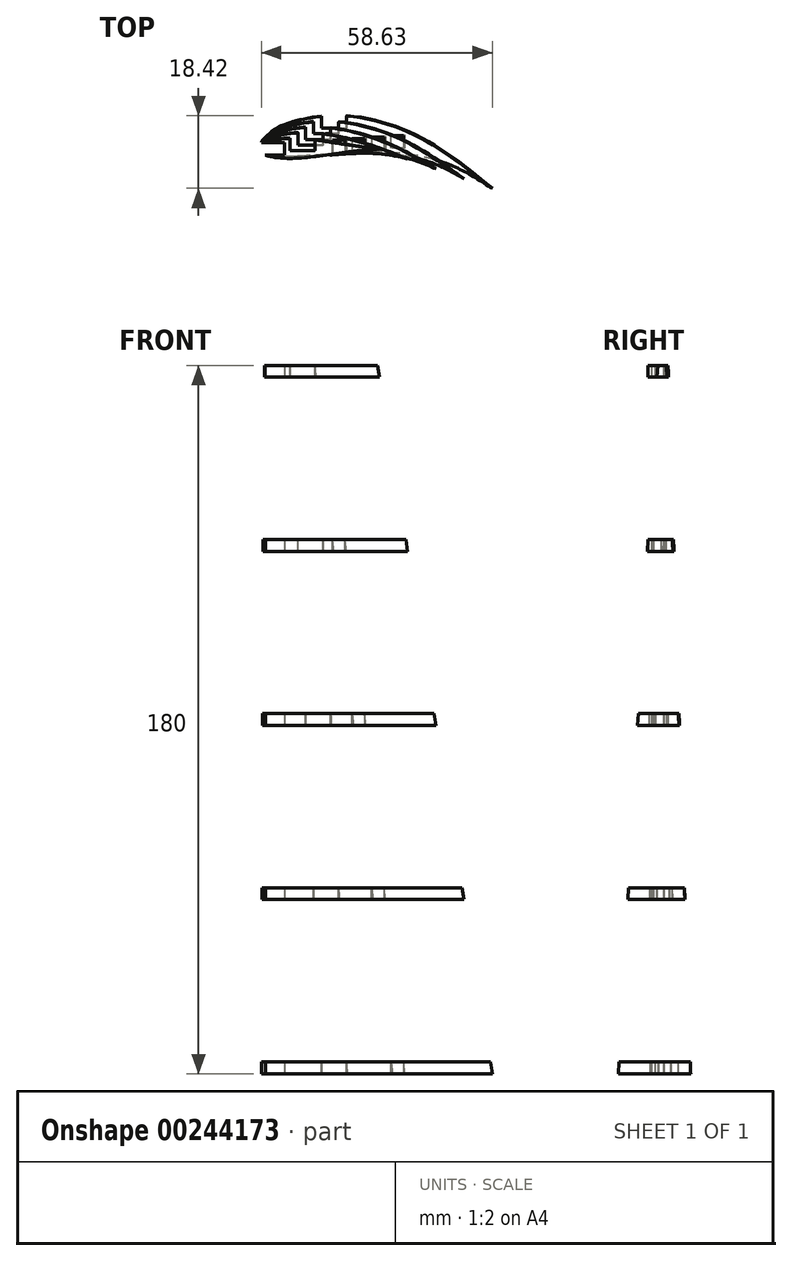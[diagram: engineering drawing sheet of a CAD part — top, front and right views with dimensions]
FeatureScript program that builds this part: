
annotation { "Feature Type Name" : "Feature", "Feature Type Description" : "" }
export const myFeature = defineFeature(function(context is Context, id is Id, definition is map)
    precondition{}
    {
        {
            var Q0;
            Q0=qCreatedBy(makeId("Top.planeOp"),FACE);
            var sketch = newSketch(context, id + "F0", { "sketchPlane" : qUnion([Q0])});
            skLineSegment(sketch, "E0", {"start": v(0.56, 2.05) * mm, "end": v(2.04, 3.44) * mm});
            skLineSegment(sketch, "E1", {"start": v(2.04, 3.44) * mm, "end": v(2.8, 4.09) * mm});
            skLineSegment(sketch, "E2", {"start": v(2.8, 4.09) * mm, "end": v(3.82, 4.84) * mm});
            skLineSegment(sketch, "E3", {"start": v(3.82, 4.84) * mm, "end": v(4.45, 5.23) * mm});
            skLineSegment(sketch, "E4", {"start": v(4.45, 5.23) * mm, "end": v(5.33, 5.7) * mm});
            skLineSegment(sketch, "E5", {"start": v(5.33, 5.7) * mm, "end": v(6.25, 6.12) * mm});
            skLineSegment(sketch, "E6", {"start": v(6.25, 6.12) * mm, "end": v(7.2, 6.48) * mm});
            skLineSegment(sketch, "E7", {"start": v(7.2, 6.48) * mm, "end": v(8.16, 6.8) * mm});
            skLineSegment(sketch, "E8", {"start": v(8.16, 6.8) * mm, "end": v(9.34, 7.15) * mm});
            skLineSegment(sketch, "E9", {"start": v(9.34, 7.15) * mm, "end": v(10.11, 7.36) * mm});
            skLineSegment(sketch, "E10", {"start": v(10.11, 7.36) * mm, "end": v(11.1, 7.6) * mm});
            skLineSegment(sketch, "E11", {"start": v(11.1, 7.6) * mm, "end": v(12.08, 7.8) * mm});
            skLineSegment(sketch, "E12", {"start": v(12.08, 7.8) * mm, "end": v(13.07, 7.98) * mm});
            skLineSegment(sketch, "E13", {"start": v(13.07, 7.98) * mm, "end": v(14.07, 8.14) * mm});
            skLineSegment(sketch, "E14", {"start": v(14.07, 8.14) * mm, "end": v(15.06, 8.26) * mm});
            skLineSegment(sketch, "E15", {"start": v(15.06, 8.26) * mm, "end": v(16.06, 8.36) * mm});
            skLineSegment(sketch, "E16", {"start": v(16.06, 8.36) * mm, "end": v(16.57, 8.4) * mm});
            skLineSegment(sketch, "E17", {"start": v(16.57, 8.4) * mm, "end": v(18.07, 8.47) * mm});
            skLineSegment(sketch, "E18", {"start": v(18.07, 8.47) * mm, "end": v(19.07, 8.48) * mm});
            skLineSegment(sketch, "E19", {"start": v(19.07, 8.48) * mm, "end": v(20.08, 8.46) * mm});
            skLineSegment(sketch, "E20", {"start": v(20.08, 8.46) * mm, "end": v(21.09, 8.42) * mm});
            skLineSegment(sketch, "E21", {"start": v(21.09, 8.42) * mm, "end": v(23.1, 8.25) * mm});
            skLineSegment(sketch, "E22", {"start": v(23.1, 8.25) * mm, "end": v(24.82, 8.04) * mm});
            skLineSegment(sketch, "E23", {"start": v(24.82, 8.04) * mm, "end": v(27.09, 7.66) * mm});
            skLineSegment(sketch, "E24", {"start": v(27.09, 7.66) * mm, "end": v(29.05, 7.24) * mm});
            skLineSegment(sketch, "E25", {"start": v(29.05, 7.24) * mm, "end": v(31, 6.74) * mm});
            skLineSegment(sketch, "E26", {"start": v(31, 6.74) * mm, "end": v(33.36, 6.03) * mm});
            skLineSegment(sketch, "E27", {"start": v(33.36, 6.03) * mm, "end": v(34.84, 5.51) * mm});
            skLineSegment(sketch, "E28", {"start": v(34.84, 5.51) * mm, "end": v(36.73, 4.8) * mm});
            skLineSegment(sketch, "E29", {"start": v(36.73, 4.8) * mm, "end": v(38.58, 4) * mm});
            skLineSegment(sketch, "E30", {"start": v(38.58, 4) * mm, "end": v(40.4, 3.16) * mm});
            skLineSegment(sketch, "E31", {"start": v(40.4, 3.16) * mm, "end": v(41.54, 2.59) * mm});
            skLineSegment(sketch, "E32", {"start": v(41.54, 2.59) * mm, "end": v(43.94, 1.28) * mm});
            skLineSegment(sketch, "E33", {"start": v(43.94, 1.28) * mm, "end": v(45.67, 0.26) * mm});
            skLineSegment(sketch, "E34", {"start": v(45.67, 0.26) * mm, "end": v(47.37, -0.82) * mm});
            skLineSegment(sketch, "E35", {"start": v(47.37, -0.82) * mm, "end": v(48.77, -1.74) * mm});
            skLineSegment(sketch, "E36", {"start": v(48.77, -1.74) * mm, "end": v(50.75, -3.11) * mm});
            skLineSegment(sketch, "E37", {"start": v(50.75, -3.11) * mm, "end": v(52.4, -4.32) * mm});
            skLineSegment(sketch, "E38", {"start": v(52.4, -4.32) * mm, "end": v(54.53, -6.01) * mm});
            skLineSegment(sketch, "E39", {"start": v(54.53, -6.01) * mm, "end": v(55.4, -6.76) * mm});
            skLineSegment(sketch, "E40", {"start": v(55.4, -6.76) * mm, "end": v(56.12, -7.39) * mm});
            skLineSegment(sketch, "E41", {"start": v(56.12, -7.39) * mm, "end": v(56.86, -8.05) * mm});
            skLineSegment(sketch, "E42", {"start": v(56.86, -8.05) * mm, "end": v(57.66, -8.75) * mm});
            skLineSegment(sketch, "E43", {"start": v(57.66, -8.75) * mm, "end": v(58.2, -9.21) * mm});
            skLineSegment(sketch, "E44", {"start": v(58.2, -9.21) * mm, "end": v(58.75, -9.68) * mm});
            skLineSegment(sketch, "E45", {"start": v(58.75, -9.68) * mm, "end": v(58.92, -9.83) * mm});
            skLineSegment(sketch, "E46", {"start": v(58.92, -9.83) * mm, "end": v(59.03, -9.93) * mm});
            skLineSegment(sketch, "E47", {"start": v(59.03, -9.93) * mm, "end": v(59.12, -10) * mm});
            skLineSegment(sketch, "E48", {"start": v(59.12, -10) * mm, "end": v(59.13, -10.04) * mm});
            skLineSegment(sketch, "E49", {"start": v(59.13, -10.04) * mm, "end": v(59.1, -10.02) * mm});
            skLineSegment(sketch, "E50", {"start": v(59.1, -10.02) * mm, "end": v(59, -9.97) * mm});
            skLineSegment(sketch, "E51", {"start": v(59, -9.97) * mm, "end": v(58.88, -9.89) * mm});
            skLineSegment(sketch, "E52", {"start": v(58.88, -9.89) * mm, "end": v(58.71, -9.78) * mm});
            skLineSegment(sketch, "E53", {"start": v(58.71, -9.78) * mm, "end": v(58.5, -9.64) * mm});
            skLineSegment(sketch, "E54", {"start": v(58.5, -9.64) * mm, "end": v(58.27, -9.48) * mm});
            skLineSegment(sketch, "E55", {"start": v(58.27, -9.48) * mm, "end": v(58.01, -9.3) * mm});
            skLineSegment(sketch, "E56", {"start": v(58.01, -9.3) * mm, "end": v(57.42, -8.88) * mm});
            skLineSegment(sketch, "E57", {"start": v(57.42, -8.88) * mm, "end": v(56.77, -8.43) * mm});
            skLineSegment(sketch, "E58", {"start": v(56.77, -8.43) * mm, "end": v(55.48, -7.55) * mm});
            skLineSegment(sketch, "E59", {"start": v(55.48, -7.55) * mm, "end": v(54.79, -7.1) * mm});
            skLineSegment(sketch, "E60", {"start": v(54.79, -7.1) * mm, "end": v(54.18, -6.73) * mm});
            skLineSegment(sketch, "E61", {"start": v(54.18, -6.73) * mm, "end": v(53.6, -6.38) * mm});
            skLineSegment(sketch, "E62", {"start": v(53.6, -6.38) * mm, "end": v(53.05, -6.06) * mm});
            skLineSegment(sketch, "E63", {"start": v(53.05, -6.06) * mm, "end": v(52.53, -5.78) * mm});
            skLineSegment(sketch, "E64", {"start": v(52.53, -5.78) * mm, "end": v(52.03, -5.52) * mm});
            skLineSegment(sketch, "E65", {"start": v(52.03, -5.52) * mm, "end": v(51.55, -5.29) * mm});
            skLineSegment(sketch, "E66", {"start": v(51.55, -5.29) * mm, "end": v(51.1, -5.08) * mm});
            skLineSegment(sketch, "E67", {"start": v(51.1, -5.08) * mm, "end": v(50.22, -4.72) * mm});
            skLineSegment(sketch, "E68", {"start": v(50.22, -4.72) * mm, "end": v(49.4, -4.43) * mm});
            skLineSegment(sketch, "E69", {"start": v(49.4, -4.43) * mm, "end": v(48.61, -4.18) * mm});
            skLineSegment(sketch, "E70", {"start": v(48.61, -4.18) * mm, "end": v(47.04, -3.79) * mm});
            skLineSegment(sketch, "E71", {"start": v(47.04, -3.79) * mm, "end": v(46.4, -3.64) * mm});
            skLineSegment(sketch, "E72", {"start": v(46.4, -3.64) * mm, "end": v(45.37, -3.4) * mm});
            skLineSegment(sketch, "E73", {"start": v(45.37, -3.4) * mm, "end": v(44.49, -3.2) * mm});
            skLineSegment(sketch, "E74", {"start": v(44.49, -3.2) * mm, "end": v(43.57, -2.98) * mm});
            skLineSegment(sketch, "E75", {"start": v(43.57, -2.98) * mm, "end": v(41.64, -2.54) * mm});
            skLineSegment(sketch, "E76", {"start": v(41.64, -2.54) * mm, "end": v(39.63, -2.11) * mm});
            skLineSegment(sketch, "E77", {"start": v(39.63, -2.11) * mm, "end": v(37.56, -1.7) * mm});
            skLineSegment(sketch, "E78", {"start": v(37.56, -1.7) * mm, "end": v(35.47, -1.36) * mm});
            skLineSegment(sketch, "E79", {"start": v(35.47, -1.36) * mm, "end": v(33, -1.03) * mm});
            skLineSegment(sketch, "E80", {"start": v(33, -1.03) * mm, "end": v(31.32, -0.88) * mm});
            skLineSegment(sketch, "E81", {"start": v(31.32, -0.88) * mm, "end": v(29.29, -0.77) * mm});
            skLineSegment(sketch, "E82", {"start": v(29.29, -0.77) * mm, "end": v(27.28, -0.73) * mm});
            skLineSegment(sketch, "E83", {"start": v(27.28, -0.73) * mm, "end": v(25.28, -0.76) * mm});
            skLineSegment(sketch, "E84", {"start": v(25.28, -0.76) * mm, "end": v(23.3, -0.83) * mm});
            skLineSegment(sketch, "E85", {"start": v(23.3, -0.83) * mm, "end": v(19.54, -1.03) * mm});
            skLineSegment(sketch, "E86", {"start": v(19.54, -1.03) * mm, "end": v(17.26, -1.18) * mm});
            skLineSegment(sketch, "E87", {"start": v(17.26, -1.18) * mm, "end": v(13.22, -1.47) * mm});
            skLineSegment(sketch, "E88", {"start": v(13.22, -1.47) * mm, "end": v(11.22, -1.65) * mm});
            skLineSegment(sketch, "E89", {"start": v(11.22, -1.65) * mm, "end": v(9.16, -1.86) * mm});
            skLineSegment(sketch, "E90", {"start": v(9.16, -1.86) * mm, "end": v(7.34, -2.05) * mm});
            skLineSegment(sketch, "E91", {"start": v(7.34, -2.05) * mm, "end": v(6.37, -2.12) * mm});
            skLineSegment(sketch, "E92", {"start": v(6.37, -2.12) * mm, "end": v(5.38, -2.14) * mm});
            skLineSegment(sketch, "E93", {"start": v(5.38, -2.14) * mm, "end": v(4.35, -2.1) * mm});
            skLineSegment(sketch, "E94", {"start": v(4.35, -2.1) * mm, "end": v(3.82, -2.04) * mm});
            skLineSegment(sketch, "E95", {"start": v(3.82, -2.04) * mm, "end": v(3.28, -1.96) * mm});
            skLineSegment(sketch, "E96", {"start": v(3.28, -1.96) * mm, "end": v(2.76, -1.86) * mm});
            skLineSegment(sketch, "E97", {"start": v(2.76, -1.86) * mm, "end": v(2.16, -1.72) * mm});
            skLineSegment(sketch, "E98", {"start": v(2.16, -1.72) * mm, "end": v(1.6, -1.55) * mm});
            skLineSegment(sketch, "E99", {"start": v(1.6, -1.55) * mm, "end": v(1.1, -1.34) * mm});
            skLineSegment(sketch, "E100", {"start": v(1.1, -1.34) * mm, "end": v(0.65, -1.09) * mm});
            skLineSegment(sketch, "E101", {"start": v(0.65, -1.09) * mm, "end": v(0.47, -0.94) * mm});
            skLineSegment(sketch, "E102", {"start": v(0.47, -0.94) * mm, "end": v(0.3, -0.78) * mm});
            skLineSegment(sketch, "E103", {"start": v(0.3, -0.78) * mm, "end": v(0.18, -0.6) * mm});
            skLineSegment(sketch, "E104", {"start": v(0.18, -0.6) * mm, "end": v(0.09, -0.44) * mm});
            skLineSegment(sketch, "E105", {"start": v(0.09, -0.44) * mm, "end": v(0.02, -0.22) * mm});
            skLineSegment(sketch, "E106", {"start": v(0.02, -0.22) * mm, "end": v(0, 0) * mm});
            skLineSegment(sketch, "E107", {"start": v(0, 0) * mm, "end": v(0, 0.23) * mm});
            skLineSegment(sketch, "E108", {"start": v(0, 0.23) * mm, "end": v(0.04, 0.47) * mm});
            skLineSegment(sketch, "E109", {"start": v(0.04, 0.47) * mm, "end": v(0.16, 0.98) * mm});
            skLineSegment(sketch, "E110", {"start": v(0.16, 0.98) * mm, "end": v(0.35, 1.5) * mm});
            skLineSegment(sketch, "E111", {"start": v(0.35, 1.5) * mm, "end": v(0.56, 2.05) * mm});
            skSolve(sketch);
        }
        {
            var Q0;
            Q0=qCreatedBy(makeId("Top.planeOp"),FACE);
            var sketch = newSketch(context, id + "F1", { "sketchPlane" : qUnion([Q0])});
            skPoint(sketch, "E112.0", {"position": v(0, 0) * mm});
            skPoint(sketch, "E112.1", {"position": v(0.16, 0.98) * mm});
            skPoint(sketch, "E112.2", {"position": v(5.33, 5.7) * mm});
            skPoint(sketch, "E112.3", {"position": v(19.07, 8.48) * mm});
            skPoint(sketch, "E112.4", {"position": v(40.4, 3.16) * mm});
            skPoint(sketch, "E112.5", {"position": v(59.13, -10.04) * mm});
            skPoint(sketch, "E112.6", {"position": v(27.28, -0.73) * mm});
            skPoint(sketch, "E112.7", {"position": v(2.76, -1.86) * mm});
            skPoint(sketch, "E112.8", {"position": v(0.18, -0.6) * mm});
            skPoint(sketch, "E112.9", {"position": v(0.65, -1.09) * mm});
            skFitSpline(sketch, "E113", {"points": [v(0, 0) * mm, v(0.18, -0.6) * mm, v(0.65, -1.09) * mm, v(2.76, -1.86) * mm, v(27.28, -0.73) * mm, v(59.13, -10.04) * mm], "startDerivative": vector(2.05, -11.29) * mm, "endDerivative": vector(81.04, -57.95) * mm});
            skPoint(sketch, "E114.0", {"position": v(2.04, 3.44) * mm});
            skFitSpline(sketch, "E115", {"points": [v(0, 0) * mm, v(0.16, 0.98) * mm, v(2.04, 3.44) * mm, v(5.33, 5.7) * mm, v(19.07, 8.48) * mm, v(40.4, 3.16) * mm, v(59.13, -10.04) * mm], "startDerivative": vector(-0.04, 15.95) * mm, "endDerivative": vector(66.9, -54.86) * mm});
            skSolve(sketch);
        }
        {
            var Q0;
            Q0=qCreatedBy(makeId("Top.planeOp"),FACE);
            cPlane(context, id + "F2", {"entities" : qUnion([Q0]), "cplaneType" : CPlaneType.OFFSET, "offset" : 180 * mm, "width" : 150 * mm, "height" : 150 * mm});
        }
        {
            var Q0;
            Q0=qCreatedBy(id+"F2.planeOp",FACE);
            var sketch = newSketch(context, id + "F3", { "sketchPlane" : qUnion([Q0])});
            skLineSegment(sketch, "E116", {"start": v(0, 0) * mm, "end": v(0.23, 0.44) * mm});
            skLineSegment(sketch, "E117", {"start": v(0.23, 0.44) * mm, "end": v(0.36, 0.65) * mm});
            skLineSegment(sketch, "E118", {"start": v(0.36, 0.65) * mm, "end": v(0.5, 0.85) * mm});
            skLineSegment(sketch, "E119", {"start": v(0.5, 0.85) * mm, "end": v(0.64, 1.04) * mm});
            skLineSegment(sketch, "E120", {"start": v(0.64, 1.04) * mm, "end": v(0.77, 1.18) * mm});
            skLineSegment(sketch, "E121", {"start": v(0.77, 1.18) * mm, "end": v(0.98, 1.36) * mm});
            skLineSegment(sketch, "E122", {"start": v(0.98, 1.36) * mm, "end": v(1.17, 1.5) * mm});
            skLineSegment(sketch, "E123", {"start": v(1.17, 1.5) * mm, "end": v(1.38, 1.62) * mm});
            skLineSegment(sketch, "E124", {"start": v(1.38, 1.62) * mm, "end": v(1.6, 1.72) * mm});
            skLineSegment(sketch, "E125", {"start": v(1.6, 1.72) * mm, "end": v(1.82, 1.81) * mm});
            skLineSegment(sketch, "E126", {"start": v(1.82, 1.81) * mm, "end": v(2.06, 1.9) * mm});
            skLineSegment(sketch, "E127", {"start": v(2.06, 1.9) * mm, "end": v(2.55, 2.03) * mm});
            skLineSegment(sketch, "E128", {"start": v(2.55, 2.03) * mm, "end": v(2.95, 2.13) * mm});
            skLineSegment(sketch, "E129", {"start": v(2.95, 2.13) * mm, "end": v(3.53, 2.24) * mm});
            skLineSegment(sketch, "E130", {"start": v(3.53, 2.24) * mm, "end": v(4.01, 2.33) * mm});
            skLineSegment(sketch, "E131", {"start": v(4.01, 2.33) * mm, "end": v(4.97, 2.47) * mm});
            skLineSegment(sketch, "E132", {"start": v(4.97, 2.47) * mm, "end": v(5.92, 2.57) * mm});
            skLineSegment(sketch, "E133", {"start": v(5.92, 2.57) * mm, "end": v(6.44, 2.6) * mm});
            skLineSegment(sketch, "E134", {"start": v(6.44, 2.6) * mm, "end": v(7.84, 2.63) * mm});
            skLineSegment(sketch, "E135", {"start": v(7.84, 2.63) * mm, "end": v(8.81, 2.62) * mm});
            skLineSegment(sketch, "E136", {"start": v(8.81, 2.62) * mm, "end": v(9.78, 2.58) * mm});
            skLineSegment(sketch, "E137", {"start": v(9.78, 2.58) * mm, "end": v(10.87, 2.51) * mm});
            skLineSegment(sketch, "E138", {"start": v(10.87, 2.51) * mm, "end": v(11.73, 2.44) * mm});
            skLineSegment(sketch, "E139", {"start": v(11.73, 2.44) * mm, "end": v(12.7, 2.36) * mm});
            skLineSegment(sketch, "E140", {"start": v(12.7, 2.36) * mm, "end": v(13.67, 2.26) * mm});
            skLineSegment(sketch, "E141", {"start": v(13.67, 2.26) * mm, "end": v(14.63, 2.14) * mm});
            skLineSegment(sketch, "E142", {"start": v(14.63, 2.14) * mm, "end": v(15.89, 1.98) * mm});
            skLineSegment(sketch, "E143", {"start": v(15.89, 1.98) * mm, "end": v(16.53, 1.89) * mm});
            skLineSegment(sketch, "E144", {"start": v(16.53, 1.89) * mm, "end": v(18.42, 1.6) * mm});
            skLineSegment(sketch, "E145", {"start": v(18.42, 1.6) * mm, "end": v(19.38, 1.44) * mm});
            skLineSegment(sketch, "E146", {"start": v(19.38, 1.44) * mm, "end": v(20.35, 1.28) * mm});
            skLineSegment(sketch, "E147", {"start": v(20.35, 1.28) * mm, "end": v(21, 1.18) * mm});
            skLineSegment(sketch, "E148", {"start": v(21, 1.18) * mm, "end": v(22.34, 0.98) * mm});
            skLineSegment(sketch, "E149", {"start": v(22.34, 0.98) * mm, "end": v(23.33, 0.83) * mm});
            skLineSegment(sketch, "E150", {"start": v(23.33, 0.83) * mm, "end": v(24.3, 0.68) * mm});
            skLineSegment(sketch, "E151", {"start": v(24.3, 0.68) * mm, "end": v(24.75, 0.61) * mm});
            skLineSegment(sketch, "E152", {"start": v(24.75, 0.61) * mm, "end": v(25.2, 0.54) * mm});
            skLineSegment(sketch, "E153", {"start": v(25.2, 0.54) * mm, "end": v(25.57, 0.47) * mm});
            skLineSegment(sketch, "E154", {"start": v(25.57, 0.47) * mm, "end": v(26.03, 0.39) * mm});
            skLineSegment(sketch, "E155", {"start": v(26.03, 0.39) * mm, "end": v(26.44, 0.32) * mm});
            skLineSegment(sketch, "E156", {"start": v(26.44, 0.32) * mm, "end": v(26.87, 0.25) * mm});
            skLineSegment(sketch, "E157", {"start": v(26.87, 0.25) * mm, "end": v(27.33, 0.19) * mm});
            skLineSegment(sketch, "E158", {"start": v(27.33, 0.19) * mm, "end": v(27.57, 0.16) * mm});
            skLineSegment(sketch, "E159", {"start": v(27.57, 0.16) * mm, "end": v(27.84, 0.13) * mm});
            skLineSegment(sketch, "E160", {"start": v(27.84, 0.13) * mm, "end": v(28.12, 0.1) * mm});
            skLineSegment(sketch, "E161", {"start": v(28.12, 0.1) * mm, "end": v(28.42, 0.08) * mm});
            skLineSegment(sketch, "E162", {"start": v(28.42, 0.08) * mm, "end": v(28.8, 0.06) * mm});
            skLineSegment(sketch, "E163", {"start": v(28.8, 0.06) * mm, "end": v(29.09, 0.04) * mm});
            skLineSegment(sketch, "E164", {"start": v(29.09, 0.04) * mm, "end": v(29.42, 0.03) * mm});
            skLineSegment(sketch, "E165", {"start": v(29.42, 0.03) * mm, "end": v(29.57, 0.02) * mm});
            skLineSegment(sketch, "E166", {"start": v(29.57, 0.02) * mm, "end": v(29.71, 0.02) * mm});
            skLineSegment(sketch, "E167", {"start": v(29.71, 0.02) * mm, "end": v(29.83, 0.01) * mm});
            skLineSegment(sketch, "E168", {"start": v(29.83, 0.01) * mm, "end": v(29.92, 0) * mm});
            skLineSegment(sketch, "E169", {"start": v(29.92, 0) * mm, "end": v(29.98, 0) * mm});
            skLineSegment(sketch, "E170", {"start": v(29.98, 0) * mm, "end": v(30, 0) * mm});
            skLineSegment(sketch, "E171", {"start": v(30, 0) * mm, "end": v(29.99, 0) * mm});
            skLineSegment(sketch, "E172", {"start": v(29.99, 0) * mm, "end": v(29.94, 0) * mm});
            skLineSegment(sketch, "E173", {"start": v(29.94, 0) * mm, "end": v(29.85, 0) * mm});
            skLineSegment(sketch, "E174", {"start": v(29.85, 0) * mm, "end": v(29.74, -0.01) * mm});
            skLineSegment(sketch, "E175", {"start": v(29.74, -0.01) * mm, "end": v(29.61, -0.01) * mm});
            skLineSegment(sketch, "E176", {"start": v(29.61, -0.01) * mm, "end": v(29.46, -0.02) * mm});
            skLineSegment(sketch, "E177", {"start": v(29.46, -0.02) * mm, "end": v(29.13, -0.02) * mm});
            skLineSegment(sketch, "E178", {"start": v(29.13, -0.02) * mm, "end": v(28.9, -0.03) * mm});
            skLineSegment(sketch, "E179", {"start": v(28.9, -0.03) * mm, "end": v(28.49, -0.04) * mm});
            skLineSegment(sketch, "E180", {"start": v(28.49, -0.04) * mm, "end": v(28.2, -0.06) * mm});
            skLineSegment(sketch, "E181", {"start": v(28.2, -0.06) * mm, "end": v(27.92, -0.07) * mm});
            skLineSegment(sketch, "E182", {"start": v(27.92, -0.07) * mm, "end": v(27.66, -0.1) * mm});
            skLineSegment(sketch, "E183", {"start": v(27.66, -0.1) * mm, "end": v(27.41, -0.11) * mm});
            skLineSegment(sketch, "E184", {"start": v(27.41, -0.11) * mm, "end": v(26.95, -0.16) * mm});
            skLineSegment(sketch, "E185", {"start": v(26.95, -0.16) * mm, "end": v(26.52, -0.2) * mm});
            skLineSegment(sketch, "E186", {"start": v(26.52, -0.2) * mm, "end": v(26.11, -0.27) * mm});
            skLineSegment(sketch, "E187", {"start": v(26.11, -0.27) * mm, "end": v(25.7, -0.32) * mm});
            skLineSegment(sketch, "E188", {"start": v(25.7, -0.32) * mm, "end": v(25.26, -0.39) * mm});
            skLineSegment(sketch, "E189", {"start": v(25.26, -0.39) * mm, "end": v(24.8, -0.45) * mm});
            skLineSegment(sketch, "E190", {"start": v(24.8, -0.45) * mm, "end": v(24.34, -0.51) * mm});
            skLineSegment(sketch, "E191", {"start": v(24.34, -0.51) * mm, "end": v(23.38, -0.65) * mm});
            skLineSegment(sketch, "E192", {"start": v(23.38, -0.65) * mm, "end": v(22.38, -0.79) * mm});
            skLineSegment(sketch, "E193", {"start": v(22.38, -0.79) * mm, "end": v(21.08, -0.97) * mm});
            skLineSegment(sketch, "E194", {"start": v(21.08, -0.97) * mm, "end": v(20.4, -1.08) * mm});
            skLineSegment(sketch, "E195", {"start": v(20.4, -1.08) * mm, "end": v(18.47, -1.37) * mm});
            skLineSegment(sketch, "E196", {"start": v(18.47, -1.37) * mm, "end": v(15.89, -1.74) * mm});
            skLineSegment(sketch, "E197", {"start": v(15.89, -1.74) * mm, "end": v(14.67, -1.9) * mm});
            skLineSegment(sketch, "E198", {"start": v(14.67, -1.9) * mm, "end": v(12.75, -2.12) * mm});
            skLineSegment(sketch, "E199", {"start": v(12.75, -2.12) * mm, "end": v(10.8, -2.3) * mm});
            skLineSegment(sketch, "E200", {"start": v(10.8, -2.3) * mm, "end": v(9.83, -2.38) * mm});
            skLineSegment(sketch, "E201", {"start": v(9.83, -2.38) * mm, "end": v(8.86, -2.44) * mm});
            skLineSegment(sketch, "E202", {"start": v(8.86, -2.44) * mm, "end": v(7.89, -2.47) * mm});
            skLineSegment(sketch, "E203", {"start": v(7.89, -2.47) * mm, "end": v(6.93, -2.47) * mm});
            skLineSegment(sketch, "E204", {"start": v(6.93, -2.47) * mm, "end": v(6.35, -2.45) * mm});
            skLineSegment(sketch, "E205", {"start": v(6.35, -2.45) * mm, "end": v(5.02, -2.34) * mm});
            skLineSegment(sketch, "E206", {"start": v(5.02, -2.34) * mm, "end": v(4.06, -2.21) * mm});
            skLineSegment(sketch, "E207", {"start": v(4.06, -2.21) * mm, "end": v(2.9, -2) * mm});
            skLineSegment(sketch, "E208", {"start": v(2.9, -2) * mm, "end": v(2.6, -1.95) * mm});
            skLineSegment(sketch, "E209", {"start": v(2.6, -1.95) * mm, "end": v(2.1, -1.83) * mm});
            skLineSegment(sketch, "E210", {"start": v(2.1, -1.83) * mm, "end": v(1.85, -1.76) * mm});
            skLineSegment(sketch, "E211", {"start": v(1.85, -1.76) * mm, "end": v(1.62, -1.68) * mm});
            skLineSegment(sketch, "E212", {"start": v(1.62, -1.68) * mm, "end": v(1.4, -1.58) * mm});
            skLineSegment(sketch, "E213", {"start": v(1.4, -1.58) * mm, "end": v(1.18, -1.47) * mm});
            skLineSegment(sketch, "E214", {"start": v(1.18, -1.47) * mm, "end": v(0.98, -1.35) * mm});
            skLineSegment(sketch, "E215", {"start": v(0.98, -1.35) * mm, "end": v(0.8, -1.2) * mm});
            skLineSegment(sketch, "E216", {"start": v(0.8, -1.2) * mm, "end": v(0.7, -1.12) * mm});
            skLineSegment(sketch, "E217", {"start": v(0.7, -1.12) * mm, "end": v(0.48, -0.86) * mm});
            skLineSegment(sketch, "E218", {"start": v(0.48, -0.86) * mm, "end": v(0.35, -0.66) * mm});
            skLineSegment(sketch, "E219", {"start": v(0.35, -0.66) * mm, "end": v(0.23, -0.44) * mm});
            skLineSegment(sketch, "E220", {"start": v(0.23, -0.44) * mm, "end": v(0, 0) * mm});
            skSolve(sketch);
        }
        {
            var Q0;
            Q0=qCreatedBy(id+"F2.planeOp",FACE);
            var sketch = newSketch(context, id + "F4", { "sketchPlane" : qUnion([Q0])});
            skPoint(sketch, "E221.0", {"position": v(0, 0) * mm});
            skPoint(sketch, "E221.1", {"position": v(0.36, 0.65) * mm});
            skPoint(sketch, "E221.2", {"position": v(0.77, 1.18) * mm});
            skPoint(sketch, "E221.3", {"position": v(1.38, 1.62) * mm});
            skPoint(sketch, "E221.4", {"position": v(0.35, -0.66) * mm});
            skPoint(sketch, "E221.5", {"position": v(0.8, -1.2) * mm});
            skPoint(sketch, "E221.6", {"position": v(1.62, -1.68) * mm});
            skPoint(sketch, "E221.7", {"position": v(7.89, -2.47) * mm});
            skPoint(sketch, "E221.8", {"position": v(7.84, 2.63) * mm});
            skPoint(sketch, "E221.9", {"position": v(21, 1.18) * mm});
            skPoint(sketch, "E221.10", {"position": v(21.08, -0.97) * mm});
            skPoint(sketch, "E221.11", {"position": v(30, 0) * mm});
            skFitSpline(sketch, "E222", {"points": [v(0, 0) * mm, v(0.36, 0.65) * mm, v(0.77, 1.18) * mm, v(1.38, 1.62) * mm, v(7.84, 2.63) * mm, v(21, 1.18) * mm, v(30, 0) * mm], "startDerivative": vector(4.6, 9.1) * mm, "endDerivative": vector(32.93, -3.87) * mm});
            skFitSpline(sketch, "E223", {"points": [v(0, 0) * mm, v(0.35, -0.66) * mm, v(0.8, -1.2) * mm, v(1.62, -1.68) * mm, v(7.89, -2.47) * mm, v(21.08, -0.97) * mm, v(30, 0) * mm], "startDerivative": vector(4.5, -9.21) * mm, "endDerivative": vector(32.84, 2.96) * mm});
            skSolve(sketch);
        }
        {
            var Q0;
            Q0 = qSketchRegion(id + "F4", true);
            var Q1;
            Q1 = qSketchRegion(id + "F1", true);
            loft(context, id + "F5", {"sheetProfilesArray" : [{ "sheetProfileEntities" : qUnion([Q0]) }, { "sheetProfileEntities" : qUnion([Q1]) }]});
        }
        {
            var Q0;
            Q0=qCreatedBy(makeId("Top.planeOp"),FACE);
            var sketch = newSketch(context, id + "F6", { "sketchPlane" : qUnion([Q0])});
            skLineSegment(sketch, "E224", {"start": v(0, 0) * mm, "end": v(6.35, 0) * mm, "construction": true});
            skLineSegment(sketch, "E225", {"start": v(6.35, 0) * mm, "end": v(6.35, 1.59) * mm});
            skLineSegment(sketch, "E226", {"start": v(6.35, 1.59) * mm, "end": v(-1.9, 1.59) * mm});
            skLineSegment(sketch, "E227", {"start": v(-1.9, 1.59) * mm, "end": v(-1.9, -1.59) * mm});
            skLineSegment(sketch, "E228", {"start": v(-1.9, -1.59) * mm, "end": v(6.35, -1.59) * mm});
            skLineSegment(sketch, "E229", {"start": v(6.35, -1.59) * mm, "end": v(6.35, 0) * mm});
            skSolve(sketch);
        }
        {
            var Q0;
            Q0 = qSketchRegion(id + "F6", true);
            extrude(context, id + "F7", {"entities" : qUnion([Q0]), "operationType" : NewBodyOperationType.REMOVE, "depth" : 200 * mm, "offsetDistance" : 25 * mm});
        }
        {
            var Q0;
            Q0=makeQuery(id+"F5.opLoft","CAP_FACE",FACE,{"disambiguationData":[OSD([makeQuery(id+"F1.imprint","IMPRINT",FACE,{"disambiguationData":[TD([[makeQuery(id+"F1.imprint","IMPRINT",EDGE,{"derivedFrom":sQuery(id+"F1.wireOp",EDGE,"E113")}),1.0]])]})])],"isStart":true});
            var sketch = newSketch(context, id + "F8", { "sketchPlane" : qUnion([Q0])});
            skLineSegment(sketch, "E230", {"start": v(19.05, -8.48) * mm, "end": v(19.05, -5.3) * mm, "construction": true});
            skLineSegment(sketch, "E231", {"start": v(19.05, -5.3) * mm, "end": v(22.22, -5.3) * mm});
            skLineSegment(sketch, "E232", {"start": v(22.22, -5.3) * mm, "end": v(22.22, -8.48) * mm});
            skLineSegment(sketch, "E233", {"start": v(22.22, -8.48) * mm, "end": v(15.87, -8.48) * mm});
            skLineSegment(sketch, "E234", {"start": v(15.87, -8.48) * mm, "end": v(15.87, -5.3) * mm});
            skLineSegment(sketch, "E235", {"start": v(15.87, -5.3) * mm, "end": v(19.05, -5.3) * mm});
            skSolve(sketch);
        }
        {
            var Q0;
            Q0=makeQuery(id+"F3.imprint","IMPRINT",FACE,{"disambiguationData":[TD([[makeQuery(id+"F3.imprint","IMPRINT",EDGE,{"derivedFrom":sQuery(id+"F3.wireOp",EDGE,"E116")}),-1.0]])]});
            var sketch = newSketch(context, id + "F9", { "sketchPlane" : qUnion([Q0])});
            skLineSegment(sketch, "E236", {"start": v(10.9, 2.65) * mm, "end": v(10.9, -0.52) * mm, "construction": true});
            skLineSegment(sketch, "E237", {"start": v(10.9, -0.52) * mm, "end": v(14.08, -0.52) * mm});
            skLineSegment(sketch, "E238", {"start": v(14.08, -0.52) * mm, "end": v(14.08, 2.65) * mm});
            skLineSegment(sketch, "E239", {"start": v(14.08, 2.65) * mm, "end": v(7.73, 2.65) * mm});
            skLineSegment(sketch, "E240", {"start": v(7.73, 2.65) * mm, "end": v(7.73, -0.52) * mm});
            skLineSegment(sketch, "E241", {"start": v(7.73, -0.52) * mm, "end": v(10.9, -0.52) * mm});
            skSolve(sketch);
        }
        {
            var Q0;
            Q0=sQuery(id+"F8.wireOp",VERTEX,"E235.start");
            var Q1;
            Q1=sQuery(id+"F8.wireOp",VERTEX,"E234.start");
            var Q2;
            Q2=sQuery(id+"F9.wireOp",VERTEX,"E241.start");
            cPlane(context, id + "F10", {"entities" : qUnion([Q0, Q1, Q2]), "cplaneType" : CPlaneType.THREE_POINT, "offset" : 25 * mm, "width" : 150 * mm, "height" : 150 * mm});
        }
        {
            var Q0;
            Q0=qCreatedBy(id+"F10.planeOp",FACE);
            var sketch = newSketch(context, id + "F11", { "sketchPlane" : qUnion([Q0])});
            skPoint(sketch, "E242.0", {"position": v(-5.3, -0.72) * mm});
            skPoint(sketch, "E242.1", {"position": v(0.52, 179.47) * mm});
            skLineSegment(sketch, "E243", {"start": v(0.52, 179.47) * mm, "end": v(-5.3, -0.72) * mm});
            skSolve(sketch);
        }
        {
            var Q0;
            Q0 = qSketchRegion(id + "F8", true);
            var Q1;
            Q1=sQuery(id+"F11.wireOp",EDGE,"E243");
            sweep(context, id + "F12", {"operationType" : NewBodyOperationType.REMOVE, "profiles" : qUnion([Q0]), "path" : qUnion([Q1])});
        }
        {
            var Q1;
            Q1 = qSketchRegion(id + "F9", true);
            var Q2;
            Q2 = qSketchRegion(id + "F8", true);
            loft(context, id + "F13", {"operationType" : NewBodyOperationType.REMOVE, "sheetProfilesArray" : [{ "sheetProfileEntities" : qUnion([Q1]) }, { "sheetProfileEntities" : qUnion([Q2]) }]});
        }
        {
            var Q0;
            Q0=makeQuery(id+"F5.opLoft","CAP_FACE",FACE,{"disambiguationData":[OSD([makeQuery(id+"F1.imprint","IMPRINT",FACE,{"disambiguationData":[TD([[makeQuery(id+"F1.imprint","IMPRINT",EDGE,{"derivedFrom":sQuery(id+"F1.wireOp",EDGE,"E113")}),1.0]])]})])],"isStart":true});
            var sketch = newSketch(context, id + "F14", { "sketchPlane" : qUnion([Q0])});
            skLineSegment(sketch, "E244.bottom", {"start": v(33.78, -0.22) * mm, "end": v(36.95, -0.22) * mm});
            skLineSegment(sketch, "E244.top", {"start": v(33.78, -3.4) * mm, "end": v(36.95, -3.4) * mm});
            skLineSegment(sketch, "E244.left", {"start": v(33.78, -0.22) * mm, "end": v(33.78, -3.4) * mm});
            skLineSegment(sketch, "E244.right", {"start": v(36.95, -0.22) * mm, "end": v(36.95, -3.4) * mm});
            skSolve(sketch);
        }
        {
            var Q0;
            Q0=qCreatedBy(makeId("Front.planeOp"),FACE);
            var sketch = newSketch(context, id + "F15", { "sketchPlane" : qUnion([Q0])});
            skLineSegment(sketch, "E245", {"start": v(0, 0) * mm, "end": v(0, 3) * mm, "construction": true});
            skLineSegment(sketch, "E246.bottom", {"start": v(0, 3) * mm, "end": v(115.63, 3) * mm});
            skLineSegment(sketch, "E246.top", {"start": v(0, 44.25) * mm, "end": v(115.63, 44.25) * mm});
            skLineSegment(sketch, "E246.left", {"start": v(0, 3) * mm, "end": v(0, 44.25) * mm});
            skLineSegment(sketch, "E246.right", {"start": v(115.63, 3) * mm, "end": v(115.63, 44.25) * mm});
            skLineSegment(sketch, "E247.0.1.0", {"start": v(115.63, 47.25) * mm, "end": v(115.63, 88.5) * mm});
            skLineSegment(sketch, "E247.0.1.1", {"start": v(0, 47.25) * mm, "end": v(0, 88.5) * mm});
            skLineSegment(sketch, "E247.0.1.2", {"start": v(0, 88.5) * mm, "end": v(115.63, 88.5) * mm});
            skLineSegment(sketch, "E247.0.1.3", {"start": v(0, 47.25) * mm, "end": v(115.63, 47.25) * mm});
            skLineSegment(sketch, "E247.0.1.4", {"start": v(0, 44.25) * mm, "end": v(0, 47.25) * mm, "construction": true});
            skLineSegment(sketch, "E247.0.2.0", {"start": v(115.63, 91.5) * mm, "end": v(115.63, 132.75) * mm});
            skLineSegment(sketch, "E247.0.2.1", {"start": v(0, 91.5) * mm, "end": v(0, 132.75) * mm});
            skLineSegment(sketch, "E247.0.2.2", {"start": v(0, 132.75) * mm, "end": v(115.63, 132.75) * mm});
            skLineSegment(sketch, "E247.0.2.3", {"start": v(0, 91.5) * mm, "end": v(115.63, 91.5) * mm});
            skLineSegment(sketch, "E247.0.2.4", {"start": v(0, 88.5) * mm, "end": v(0, 91.5) * mm, "construction": true});
            skLineSegment(sketch, "E247.0.3.0", {"start": v(115.63, 135.75) * mm, "end": v(115.63, 177) * mm});
            skLineSegment(sketch, "E247.0.3.1", {"start": v(0, 135.75) * mm, "end": v(0, 177) * mm});
            skLineSegment(sketch, "E247.0.3.2", {"start": v(0, 177) * mm, "end": v(115.63, 177) * mm});
            skLineSegment(sketch, "E247.0.3.3", {"start": v(0, 135.75) * mm, "end": v(115.63, 135.75) * mm});
            skLineSegment(sketch, "E247.0.3.4", {"start": v(0, 132.75) * mm, "end": v(0, 135.75) * mm, "construction": true});
            skLineSegment(sketch, "E247.direction1", {"start": v(0, 0) * mm, "end": v(25, 0) * mm, "construction": true});
            skLineSegment(sketch, "E247.direction2", {"start": v(0, 0) * mm, "end": v(0, 44.25) * mm, "construction": true});
            skSolve(sketch);
        }
        {
            var Q0;
            Q0 = qSketchRegion(id + "F15", true);
            extrude(context, id + "F16", {"entities" : qUnion([Q0]), "operationType" : NewBodyOperationType.REMOVE, "oppositeDirection" : true, "depth" : 100 * mm, "offsetDistance" : 25 * mm, "hasSecondDirection" : true, "secondDirectionOppositeDirection" : false, "secondDirectionDepth" : 100 * mm});
        }
        {
            var Q0;
            Q0=makeQuery(id+"F16.boolean.opBoolean","COPY",FACE,{"derivedFrom":makeQuery(id+"F16.opExtrude","SWEPT_FACE",FACE,{"disambiguationData":[OSD([sQuery(id+"F15.wireOp",EDGE,"E247.0.3.3")])]})});
            var sketch = newSketch(context, id + "F17", { "sketchPlane" : qUnion([Q0])});
            skLineSegment(sketch, "E248.bottom", {"start": v(18.56, 2.24) * mm, "end": v(21.74, 2.24) * mm});
            skLineSegment(sketch, "E248.top", {"start": v(18.56, -0.94) * mm, "end": v(21.74, -0.94) * mm});
            skLineSegment(sketch, "E248.left", {"start": v(18.56, 2.24) * mm, "end": v(18.56, -0.94) * mm});
            skLineSegment(sketch, "E248.right", {"start": v(21.74, 2.24) * mm, "end": v(21.74, -0.94) * mm});
            skSolve(sketch);
        }
        {
            var Q1;
            Q1 = qSketchRegion(id + "F14", true);
            var Q2;
            Q2 = qSketchRegion(id + "F17", true);
            loft(context, id + "F18", {"operationType" : NewBodyOperationType.REMOVE, "sheetProfilesArray" : [{ "sheetProfileEntities" : qUnion([Q1]) }, { "sheetProfileEntities" : qUnion([Q2]) }]});
        }
        {
            var Q0;
            Q0=makeQuery(id+"F5.opLoft","CAP_FACE",FACE,{"disambiguationData":[OSD([makeQuery(id+"F4.imprint","IMPRINT",FACE,{"disambiguationData":[TD([[makeQuery(id+"F4.imprint","IMPRINT",EDGE,{"derivedFrom":sQuery(id+"F4.wireOp",EDGE,"E222")}),-1.0]])]})])],"isStart":true});
            var sketch = newSketch(context, id + "F19", { "sketchPlane" : qUnion([Q0])});
            skLineSegment(sketch, "E249.0", {"start": v(7.73, 2.63) * mm, "end": v(7.73, -0.52) * mm});
            skLineSegment(sketch, "E249.1", {"start": v(7.73, -0.52) * mm, "end": v(14.08, -0.52) * mm});
            skLineSegment(sketch, "E250", {"start": v(7.73, 2.63) * mm, "end": v(7.73, 3.47) * mm});
            skLineSegment(sketch, "E251", {"start": v(7.73, 3.47) * mm, "end": v(14.08, 3.47) * mm});
            skLineSegment(sketch, "E252", {"start": v(14.08, 3.47) * mm, "end": v(14.08, -0.52) * mm});
            skSolve(sketch);
        }
        {
            var Q0;
            Q0 = qSketchRegion(id + "F19", true);
            extrude(context, id + "F20", {"entities" : qUnion([Q0]), "operationType" : NewBodyOperationType.REMOVE, "oppositeDirection" : true, "depth" : 25 * mm, "offsetDistance" : 25 * mm});
        }
        {
            var Q0;
            Q0=makeQuery(id+"F16.boolean.opBoolean","COPY",FACE,{"derivedFrom":makeQuery(id+"F16.opExtrude","SWEPT_FACE",FACE,{"disambiguationData":[OSD([sQuery(id+"F15.wireOp",EDGE,"E247.0.3.3")])]})});
            var sketch = newSketch(context, id + "F21", { "sketchPlane" : qUnion([Q0])});
            skLineSegment(sketch, "E253.0", {"start": v(9.73, 4.02) * mm, "end": v(9.73, 0.91) * mm});
            skLineSegment(sketch, "E253.1", {"start": v(9.73, 0.91) * mm, "end": v(16.08, 0.91) * mm});
            skLineSegment(sketch, "E253.2", {"start": v(18.56, 2.24) * mm, "end": v(18.56, -0.94) * mm});
            skLineSegment(sketch, "E253.3", {"start": v(21.74, -0.94) * mm, "end": v(21.74, 2.24) * mm});
            skLineSegment(sketch, "E254", {"start": v(18.56, 2.24) * mm, "end": v(21.74, 2.24) * mm});
            skLineSegment(sketch, "E255", {"start": v(18.56, -0.94) * mm, "end": v(21.74, -0.94) * mm});
            skLineSegment(sketch, "E256", {"start": v(16.08, 0.91) * mm, "end": v(16.08, 5.31) * mm});
            skLineSegment(sketch, "E257", {"start": v(16.08, 5.31) * mm, "end": v(9.73, 5.31) * mm});
            skLineSegment(sketch, "E258", {"start": v(9.73, 5.31) * mm, "end": v(9.73, 4.02) * mm});
            skSolve(sketch);
        }
        {
            var Q0;
            Q0 = qSketchRegion(id + "F21", true);
            extrude(context, id + "F22", {"entities" : qUnion([Q0]), "operationType" : NewBodyOperationType.REMOVE, "oppositeDirection" : true, "depth" : 25 * mm, "offsetDistance" : 25 * mm});
        }
        {
            var Q0;
            Q0=makeQuery(id+"F16.boolean.opBoolean","COPY",FACE,{"derivedFrom":makeQuery(id+"F16.opExtrude","SWEPT_FACE",FACE,{"disambiguationData":[OSD([sQuery(id+"F15.wireOp",EDGE,"E247.0.2.3")])]})});
            var sketch = newSketch(context, id + "F23", { "sketchPlane" : qUnion([Q0])});
            skLineSegment(sketch, "E259.0", {"start": v(11.73, 5.42) * mm, "end": v(11.73, 2.34) * mm});
            skLineSegment(sketch, "E259.1", {"start": v(11.73, 2.34) * mm, "end": v(18.08, 2.34) * mm});
            skLineSegment(sketch, "E259.2", {"start": v(23.52, -0.56) * mm, "end": v(23.52, 2.61) * mm});
            skLineSegment(sketch, "E259.3", {"start": v(26.7, 2.61) * mm, "end": v(26.7, -0.56) * mm});
            skLineSegment(sketch, "E260", {"start": v(11.73, 5.42) * mm, "end": v(11.73, 7.92) * mm});
            skLineSegment(sketch, "E261", {"start": v(11.73, 7.92) * mm, "end": v(18.08, 7.92) * mm});
            skLineSegment(sketch, "E262", {"start": v(18.08, 7.92) * mm, "end": v(18.08, 2.34) * mm});
            skLineSegment(sketch, "E263", {"start": v(23.52, 2.61) * mm, "end": v(26.7, 2.61) * mm});
            skLineSegment(sketch, "E264", {"start": v(26.7, -0.56) * mm, "end": v(23.52, -0.56) * mm});
            skSolve(sketch);
        }
        {
            var Q0;
            Q0 = qSketchRegion(id + "F23", true);
            extrude(context, id + "F24", {"entities" : qUnion([Q0]), "operationType" : NewBodyOperationType.REMOVE, "oppositeDirection" : true, "depth" : 25 * mm, "offsetDistance" : 25 * mm});
        }
        {
            var Q0;
            Q0=makeQuery(id+"F16.boolean.opBoolean","COPY",FACE,{"derivedFrom":makeQuery(id+"F16.opExtrude","SWEPT_FACE",FACE,{"disambiguationData":[OSD([sQuery(id+"F15.wireOp",EDGE,"E247.0.1.3")])]})});
            var sketch = newSketch(context, id + "F25", { "sketchPlane" : qUnion([Q0])});
            skLineSegment(sketch, "E265.0", {"start": v(13.73, 6.8) * mm, "end": v(13.73, 3.77) * mm});
            skLineSegment(sketch, "E265.1", {"start": v(13.73, 3.77) * mm, "end": v(20.08, 3.77) * mm});
            skLineSegment(sketch, "E265.2", {"start": v(28.48, -0.19) * mm, "end": v(28.48, 2.99) * mm});
            skLineSegment(sketch, "E265.3", {"start": v(31.66, -0.19) * mm, "end": v(28.48, -0.19) * mm});
            skLineSegment(sketch, "E266", {"start": v(13.73, 6.8) * mm, "end": v(13.73, 9.47) * mm});
            skLineSegment(sketch, "E267", {"start": v(13.73, 9.47) * mm, "end": v(20.08, 9.47) * mm});
            skLineSegment(sketch, "E268", {"start": v(20.08, 9.47) * mm, "end": v(20.08, 3.77) * mm});
            skLineSegment(sketch, "E269", {"start": v(28.48, 2.99) * mm, "end": v(31.66, 2.99) * mm});
            skLineSegment(sketch, "E270", {"start": v(31.66, 2.99) * mm, "end": v(31.66, -0.19) * mm});
            skSolve(sketch);
        }
        {
            var Q0;
            Q0 = qSketchRegion(id + "F25", true);
            extrude(context, id + "F26", {"entities" : qUnion([Q0]), "operationType" : NewBodyOperationType.REMOVE, "oppositeDirection" : true, "depth" : 25 * mm, "offsetDistance" : 25 * mm});
        }
        {
            var Q0;
            Q0=makeQuery(id+"F16.boolean.opBoolean","COPY",FACE,{"derivedFrom":makeQuery(id+"F16.opExtrude","SWEPT_FACE",FACE,{"disambiguationData":[OSD([sQuery(id+"F15.wireOp",EDGE,"E246.bottom")])]})});
            var sketch = newSketch(context, id + "F27", { "sketchPlane" : qUnion([Q0])});
            skLineSegment(sketch, "E271.0", {"start": v(15.74, 8.2) * mm, "end": v(15.74, 5.2) * mm});
            skLineSegment(sketch, "E271.1", {"start": v(15.74, 5.2) * mm, "end": v(22.09, 5.2) * mm});
            skLineSegment(sketch, "E271.2", {"start": v(33.44, 0.19) * mm, "end": v(33.44, 3.36) * mm});
            skLineSegment(sketch, "E271.3", {"start": v(36.62, 0.19) * mm, "end": v(33.44, 0.19) * mm});
            skLineSegment(sketch, "E272", {"start": v(15.74, 8.2) * mm, "end": v(15.74, 10.26) * mm});
            skLineSegment(sketch, "E273", {"start": v(15.74, 10.26) * mm, "end": v(22.09, 10.26) * mm});
            skLineSegment(sketch, "E274", {"start": v(22.09, 10.26) * mm, "end": v(22.09, 5.2) * mm});
            skLineSegment(sketch, "E275", {"start": v(33.44, 3.36) * mm, "end": v(36.62, 3.36) * mm});
            skLineSegment(sketch, "E276", {"start": v(36.62, 3.36) * mm, "end": v(36.62, 0.19) * mm});
            skSolve(sketch);
        }
        {
            var Q0;
            Q0 = qSketchRegion(id + "F27", true);
            extrude(context, id + "F28", {"entities" : qUnion([Q0]), "operationType" : NewBodyOperationType.REMOVE, "oppositeDirection" : true, "depth" : 25 * mm, "offsetDistance" : 25 * mm});
        }
    });
